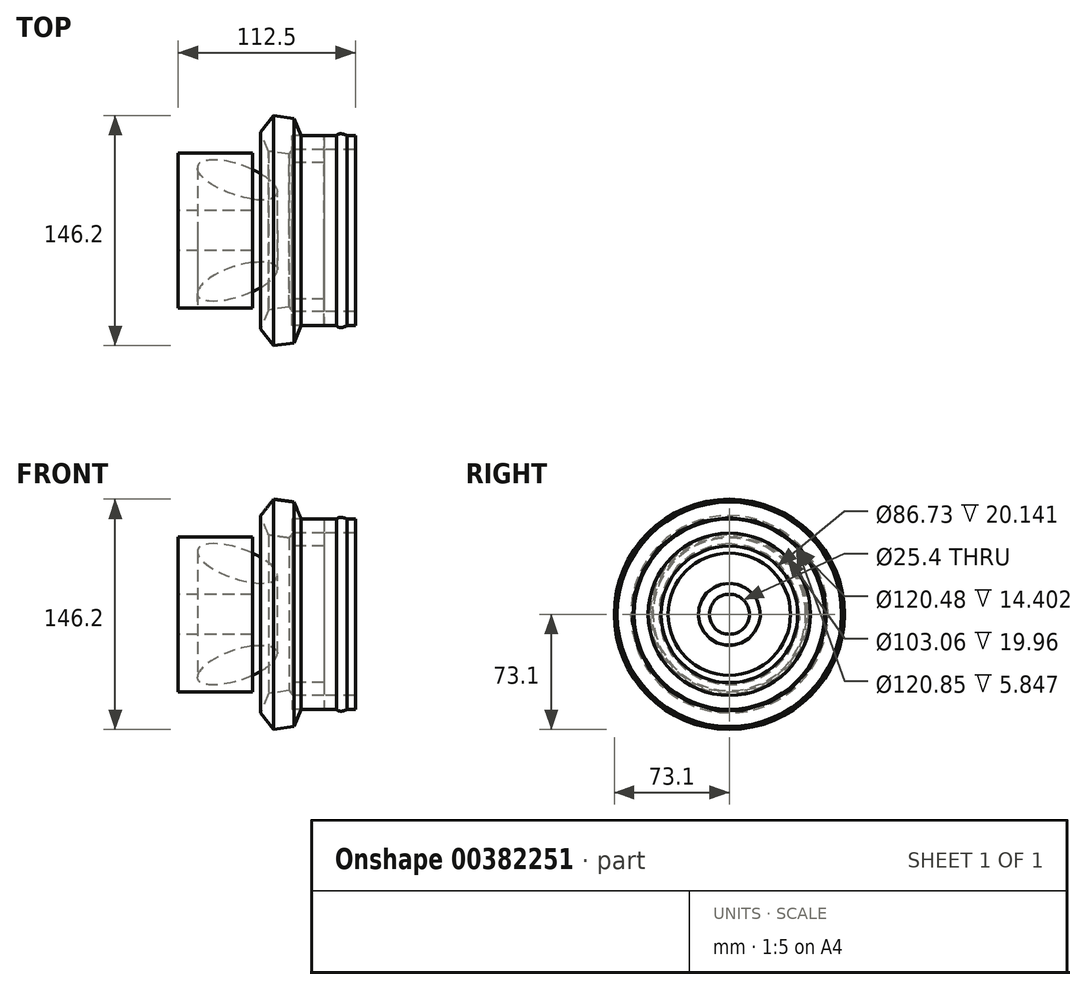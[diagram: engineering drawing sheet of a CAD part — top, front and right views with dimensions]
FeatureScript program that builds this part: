
annotation { "Feature Type Name" : "Feature", "Feature Type Description" : "" }
export const myFeature = defineFeature(function(context is Context, id is Id, definition is map)
    precondition{}
    {
        {
            var Q0;
            Q0=qCreatedBy(makeId("Front.planeOp"),FACE);
            var sketch = newSketch(context, id + "F0", { "sketchPlane" : qUnion([Q0])});
            skLineSegment(sketch, "E0", {"start": v(-70.95, 0) * mm, "end": v(68.59, 0) * mm, "construction": true});
            skLineSegment(sketch, "E1.bottom", {"start": v(-65.5, 49.17) * mm, "end": v(-18.33, 49.17) * mm});
            skLineSegment(sketch, "E1.top", {"start": v(-65.5, 12.7) * mm, "end": v(-18.33, 12.7) * mm});
            skLineSegment(sketch, "E1.left", {"start": v(-65.5, 49.17) * mm, "end": v(-65.5, 12.7) * mm});
            skLineSegment(sketch, "E1.right", {"start": v(-18.33, 49.17) * mm, "end": v(-18.33, 12.7) * mm});
            skEllipse(sketch, "E2", {"center": v(-27.94, 32.3) * mm, "majorRadius": 26.68 * mm, "minorRadius": 9.64 * mm, "majorAxis": v(0.95, -0.33)});
            skCircle(sketch, "E3.cCircle", {"center": v(0, 60.79) * mm, "radius": 11.5 * mm, "construction": true});
            skLineSegment(sketch, "E3.0", {"start": v(13.16, 58.95) * mm, "end": v(4.99, 48.47) * mm});
            skLineSegment(sketch, "E3.1", {"start": v(4.99, 48.47) * mm, "end": v(-8.17, 50.31) * mm});
            skLineSegment(sketch, "E3.2", {"start": v(-8.17, 50.31) * mm, "end": v(-13.16, 62.62) * mm});
            skLineSegment(sketch, "E3.3", {"start": v(-13.16, 62.62) * mm, "end": v(-4.99, 73.1) * mm});
            skLineSegment(sketch, "E3.4", {"start": v(-4.99, 73.1) * mm, "end": v(8.17, 71.26) * mm});
            skLineSegment(sketch, "E3.5", {"start": v(8.17, 71.26) * mm, "end": v(13.16, 58.95) * mm});
            skPoint(sketch, "E3.0.midPoint", {"position": v(9.07, 53.7) * mm});
            skLineSegment(sketch, "E4.bottom", {"start": v(27.04, 43.37) * mm, "end": v(6.9, 43.37) * mm});
            skLineSegment(sketch, "E4.top", {"start": v(27.04, 60.24) * mm, "end": v(6.9, 60.24) * mm});
            skLineSegment(sketch, "E4.left", {"start": v(27.04, 43.37) * mm, "end": v(27.04, 60.24) * mm});
            skLineSegment(sketch, "E4.right", {"start": v(6.9, 43.37) * mm, "end": v(6.9, 60.24) * mm});
            skLineSegment(sketch, "E5.bottom", {"start": v(6.71, 60.42) * mm, "end": v(47, 60.42) * mm});
            skLineSegment(sketch, "E5.top", {"start": v(6.71, 51.53) * mm, "end": v(47, 51.53) * mm});
            skLineSegment(sketch, "E5.left", {"start": v(6.71, 60.42) * mm, "end": v(6.71, 51.53) * mm});
            skLineSegment(sketch, "E5.right", {"start": v(47, 60.42) * mm, "end": v(47, 51.53) * mm});
            skEllipse(sketch, "E6", {"center": v(41, 55.98) * mm, "majorRadius": 7.46 * mm, "minorRadius": 4.17 * mm, "majorAxis": v(0.8, -0.6)});
            skPoint(sketch, "E6.centerSnap0", {"position": v(47, 55.98) * mm});
            skSolve(sketch);
        }
        {
            var Q0;
            {var subQ1=sQuery(id+"F0.wireOp",EDGE,"E1.bottom");Q0=makeQuery(id+"F0.imprint","IMPRINT",FACE,{"disambiguationData":[TD([[makeQuery(id+"F0.imprint","IMPRINT",EDGE,{"derivedFrom":subQ1}),-1.0]])]});}
            var Q1;
            {var subQ6=sQuery(id+"F0.wireOp",EDGE,"E3.1");Q1=makeQuery(id+"F0.imprint","IMPRINT",FACE,{"disambiguationData":[TD([[makeQuery(id+"F0.imprint","IMPRINT",EDGE,{"derivedFrom":subQ6}),-1.0]])]});}
            var Q2;
            {var subQ1=sQuery(id+"F0.wireOp",EDGE,"E4.bottom");Q2=makeQuery(id+"F0.imprint","IMPRINT",FACE,{"disambiguationData":[TD([[makeQuery(id+"F0.imprint","IMPRINT",EDGE,{"derivedFrom":subQ1}),-1.0]])]});}
            var Q3;
            {var subQ0=sQuery(id+"F0.wireOp",EDGE,"E6");var subQ5=sQuery(id+"F0.wireOp",EDGE,"E5.bottom");var subQ7=makeQuery(id+"F0.imprint","INTERSECT",VERTEX,{"disambiguationData":[OD(0.0)],"derivedFrom":[subQ5,subQ0]});Q3=makeQuery(id+"F0.imprint","IMPRINT",FACE,{"disambiguationData":[TD([[makeQuery(id+"F0.imprint","IMPRINT",EDGE,{"disambiguationData":[TD([[subQ7,-1.0]])],"derivedFrom":subQ5}),-1.0]])]});}
            var Q4;
            {var subQ0=sQuery(id+"F0.wireOp",EDGE,"E5.bottom");var subQ1=sQuery(id+"F0.wireOp",EDGE,"E3.5");var subQ2=makeQuery(id+"F0.imprint","INTERSECT",VERTEX,{"derivedFrom":[subQ1,subQ0]});Q4=makeQuery(id+"F0.imprint","IMPRINT",FACE,{"disambiguationData":[TD([[makeQuery(id+"F0.imprint","IMPRINT",EDGE,{"disambiguationData":[TD([[subQ2,-1.0]])],"derivedFrom":subQ1}),1.0]])]});}
            var Q5;
            {var subQ0=sQuery(id+"F0.wireOp",EDGE,"E5.right");var subQ1=sQuery(id+"F0.wireOp",EDGE,"E5.bottom");var subQ2=makeQuery(id+"F0.imprint","INTERSECT",VERTEX,{"derivedFrom":[subQ1,subQ0]});Q5=makeQuery(id+"F0.imprint","IMPRINT",FACE,{"disambiguationData":[TD([[makeQuery(id+"F0.imprint","IMPRINT",EDGE,{"disambiguationData":[TD([[subQ2,1.0]])],"derivedFrom":subQ1}),-1.0]])]});}
            var Q6;
            {var subQ0=sQuery(id+"F0.wireOp",EDGE,"E6");var subQ1=sQuery(id+"F0.wireOp",EDGE,"E5.bottom");var subQ2=makeQuery(id+"F0.imprint","INTERSECT",VERTEX,{"disambiguationData":[OD(0.0)],"derivedFrom":[subQ1,subQ0]});Q6=makeQuery(id+"F0.imprint","IMPRINT",FACE,{"disambiguationData":[TD([[makeQuery(id+"F0.imprint","IMPRINT",EDGE,{"disambiguationData":[TD([[subQ2,-1.0]])],"derivedFrom":subQ1}),1.0]])]});}
            var Q7;
            {var subQ0=sQuery(id+"F0.wireOp",EDGE,"E2");var subQ1=sQuery(id+"F0.wireOp",EDGE,"E1.right");var subQ2=makeQuery(id+"F0.imprint","INTERSECT",VERTEX,{"disambiguationData":[OD(0.0)],"derivedFrom":[subQ1,subQ0]});Q7=makeQuery(id+"F0.imprint","IMPRINT",FACE,{"disambiguationData":[TD([[makeQuery(id+"F0.imprint","IMPRINT",EDGE,{"disambiguationData":[TD([[subQ2,-1.0]])],"derivedFrom":subQ1}),1.0]])]});}
            var Q8;
            Q8=sQuery(id+"F0.wireOp",EDGE,"E0");
            revolve(context, id + "F1", {"entities" : qUnion([Q0, Q1, Q2, Q3, Q4, Q5, Q6, Q7]), "axis" : qUnion([Q8]), "revolveType" : RevolveType.FULL});
        }
    });
